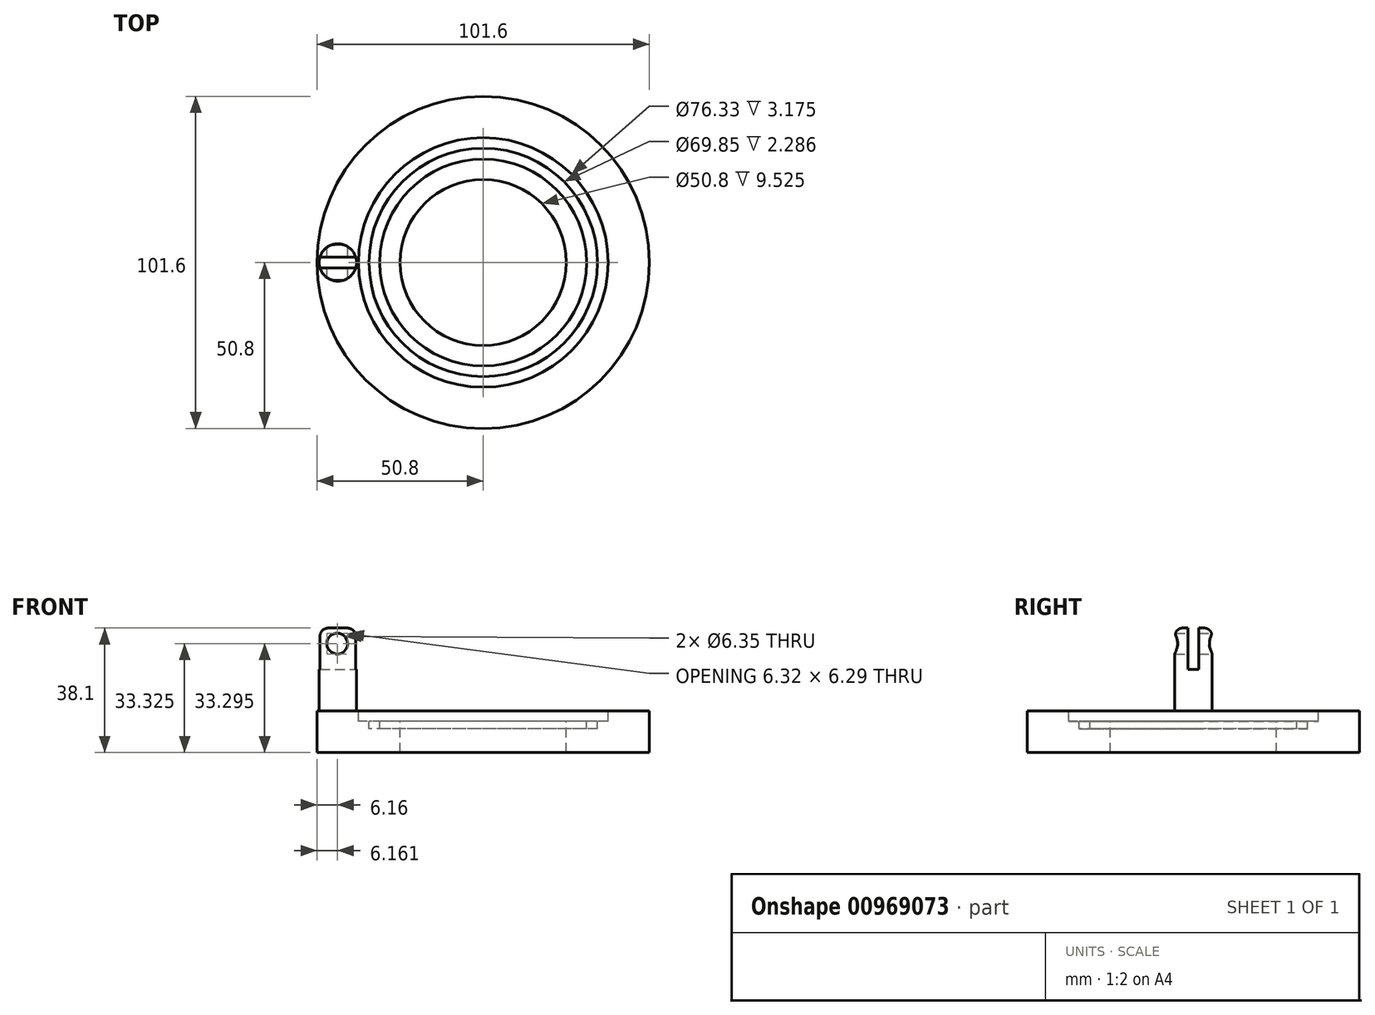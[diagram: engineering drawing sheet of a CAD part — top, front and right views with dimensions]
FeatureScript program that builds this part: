
annotation { "Feature Type Name" : "Feature", "Feature Type Description" : "" }
export const myFeature = defineFeature(function(context is Context, id is Id, definition is map)
    precondition{}
    {
        {
            var Q0;
            Q0=qCreatedBy(makeId("Top.planeOp"),FACE);
            var sketch = newSketch(context, id + "F0", { "sketchPlane" : qUnion([Q0])});
            skCircle(sketch, "E0", {"center": v(0, 0) * mm, "radius": 50.8 * mm});
            skSolve(sketch);
        }
        {
            var Q0;
            Q0 = qSketchRegion(id + "F0", true);
            extrude(context, id + "F1", {"entities" : qUnion([Q0]), "depth" : 12.7 * mm, "offsetDistance" : 25.4 * mm});
        }
        {
            var Q0;
            Q0=makeQuery(id+"F1.opExtrude","CAP_FACE",FACE,{"disambiguationData":[OSD([sQuery(id+"F0.wireOp",EDGE,"E0")])],"isStart":false});
            var sketch = newSketch(context, id + "F2", { "sketchPlane" : qUnion([Q0])});
            skCircle(sketch, "E1", {"center": v(0, 0) * mm, "radius": 38.16 * mm});
            skSolve(sketch);
        }
        {
            var Q0;
            Q0 = qSketchRegion(id + "F2", true);
            extrude(context, id + "F3", {"entities" : qUnion([Q0]), "operationType" : NewBodyOperationType.REMOVE, "oppositeDirection" : true, "depth" : 3.17 * mm, "offsetDistance" : 25.4 * mm});
        }
        {
            var Q0;
            Q0=makeQuery(id+"F3.boolean.opBoolean","COPY",FACE,{"derivedFrom":makeQuery(id+"F3.opExtrude","CAP_FACE",FACE,{"disambiguationData":[OSD([sQuery(id+"F2.wireOp",EDGE,"E1")])],"isStart":false})});
            var sketch = newSketch(context, id + "F4", { "sketchPlane" : qUnion([Q0])});
            skCircle(sketch, "E2", {"center": v(0, 0) * mm, "radius": 34.93 * mm});
            skCircle(sketch, "E3", {"center": v(0, 0) * mm, "radius": 31.62 * mm});
            skCircle(sketch, "E4", {"center": v(0, 0) * mm, "radius": 25.4 * mm});
            skSolve(sketch);
        }
        {
            var Q0;
            Q0=makeQuery(id+"F4.imprint","IMPRINT",FACE,{"disambiguationData":[TD([[makeQuery(id+"F4.imprint","IMPRINT",EDGE,{"derivedFrom":sQuery(id+"F4.wireOp",EDGE,"E2")}),1.0]])]});
            extrude(context, id + "F5", {"entities" : qUnion([Q0]), "operationType" : NewBodyOperationType.REMOVE, "oppositeDirection" : true, "depth" : 2.3 * mm, "offsetDistance" : 25.4 * mm});
        }
        {
            var Q0;
            Q0=makeQuery(id+"F4.imprint","IMPRINT",FACE,{"disambiguationData":[TD([[makeQuery(id+"F4.imprint","IMPRINT",EDGE,{"derivedFrom":sQuery(id+"F4.wireOp",EDGE,"E4")}),1.0]])]});
            extrude(context, id + "F6", {"entities" : qUnion([Q0]), "operationType" : NewBodyOperationType.REMOVE, "endBound" : BoundingType.THROUGH_ALL, "oppositeDirection" : true, "depth" : 25.4 * mm, "offsetDistance" : 25.4 * mm});
        }
        {
            var Q0;
            Q0=qCreatedBy(makeId("Top.planeOp"),FACE);
            cPlane(context, id + "F7", {"entities" : qUnion([Q0]), "cplaneType" : CPlaneType.OFFSET, "offset" : 12.7 * mm, "width" : 152.4 * mm, "height" : 152.4 * mm});
        }
        {
            var Q0;
            Q0=qCreatedBy(id+"F7.planeOp",FACE);
            var sketch = newSketch(context, id + "F8", { "sketchPlane" : qUnion([Q0])});
            skCircle(sketch, "E5", {"center": v(-44.45, 0) * mm, "radius": 5.72 * mm});
            skSolve(sketch);
        }
        {
            var Q0;
            Q0=makeQuery(id+"F8.imprint","IMPRINT",FACE,{"disambiguationData":[TD([[makeQuery(id+"F8.imprint","IMPRINT",EDGE,{"derivedFrom":sQuery(id+"F8.wireOp",EDGE,"E5")}),1.0]])]});
            extrude(context, id + "F9", {"entities" : qUnion([Q0]), "operationType" : NewBodyOperationType.ADD, "depth" : 25.4 * mm, "offsetDistance" : 25.4 * mm});
        }
        {
            var Q0;
            Q0=qCreatedBy(makeId("Front.planeOp"),FACE);
            var sketch = newSketch(context, id + "F10", { "sketchPlane" : qUnion([Q0])});
            skCircle(sketch, "E6", {"center": v(-44.64, 33.32) * mm, "radius": 3.18 * mm});
            skSolve(sketch);
        }
        {
            var Q0;
            Q0 = qSketchRegion(id + "F10", true);
            extrude(context, id + "F11", {"entities" : qUnion([Q0]), "operationType" : NewBodyOperationType.REMOVE, "endBound" : BoundingType.THROUGH_ALL, "depth" : 25.4 * mm, "offsetDistance" : 25.4 * mm, "hasSecondDirection" : true, "secondDirectionOppositeDirection" : true, "secondDirectionDepth" : 25.4 * mm});
        }
        {
            var Q0;
            Q0=makeQuery(id+"F9.opExtrude","CAP_EDGE",EDGE,{"disambiguationData":[OSD([sQuery(id+"F8.wireOp",EDGE,"E5")])],"isStart":false});
            fillet(context, id + "F12", {"entities" : qUnion([Q0]), "radius" : 2.54 * mm, "tangentPropagation" : true, "allowEdgeOverflow" : false});
        }
        {
            var Q0;
            Q0=qCreatedBy(makeId("Right.planeOp"),FACE);
            var sketch = newSketch(context, id + "F13", { "sketchPlane" : qUnion([Q0])});
            skLineSegment(sketch, "E7.bottom", {"start": v(1.65, 41.2) * mm, "end": v(-1.65, 41.2) * mm});
            skLineSegment(sketch, "E7.top", {"start": v(1.65, 25.4) * mm, "end": v(-1.65, 25.4) * mm});
            skLineSegment(sketch, "E7.left", {"start": v(1.65, 41.2) * mm, "end": v(1.65, 25.4) * mm});
            skLineSegment(sketch, "E7.right", {"start": v(-1.65, 41.2) * mm, "end": v(-1.65, 25.4) * mm});
            skPoint(sketch, "E7.middle", {"position": v(0, 33.3) * mm});
            skSolve(sketch);
        }
        {
            var Q0;
            Q0 = qSketchRegion(id + "F13", true);
            extrude(context, id + "F14", {"entities" : qUnion([Q0]), "operationType" : NewBodyOperationType.REMOVE, "endBound" : BoundingType.THROUGH_ALL, "oppositeDirection" : true, "depth" : 25.4 * mm, "offsetDistance" : 25.4 * mm});
        }
    });
